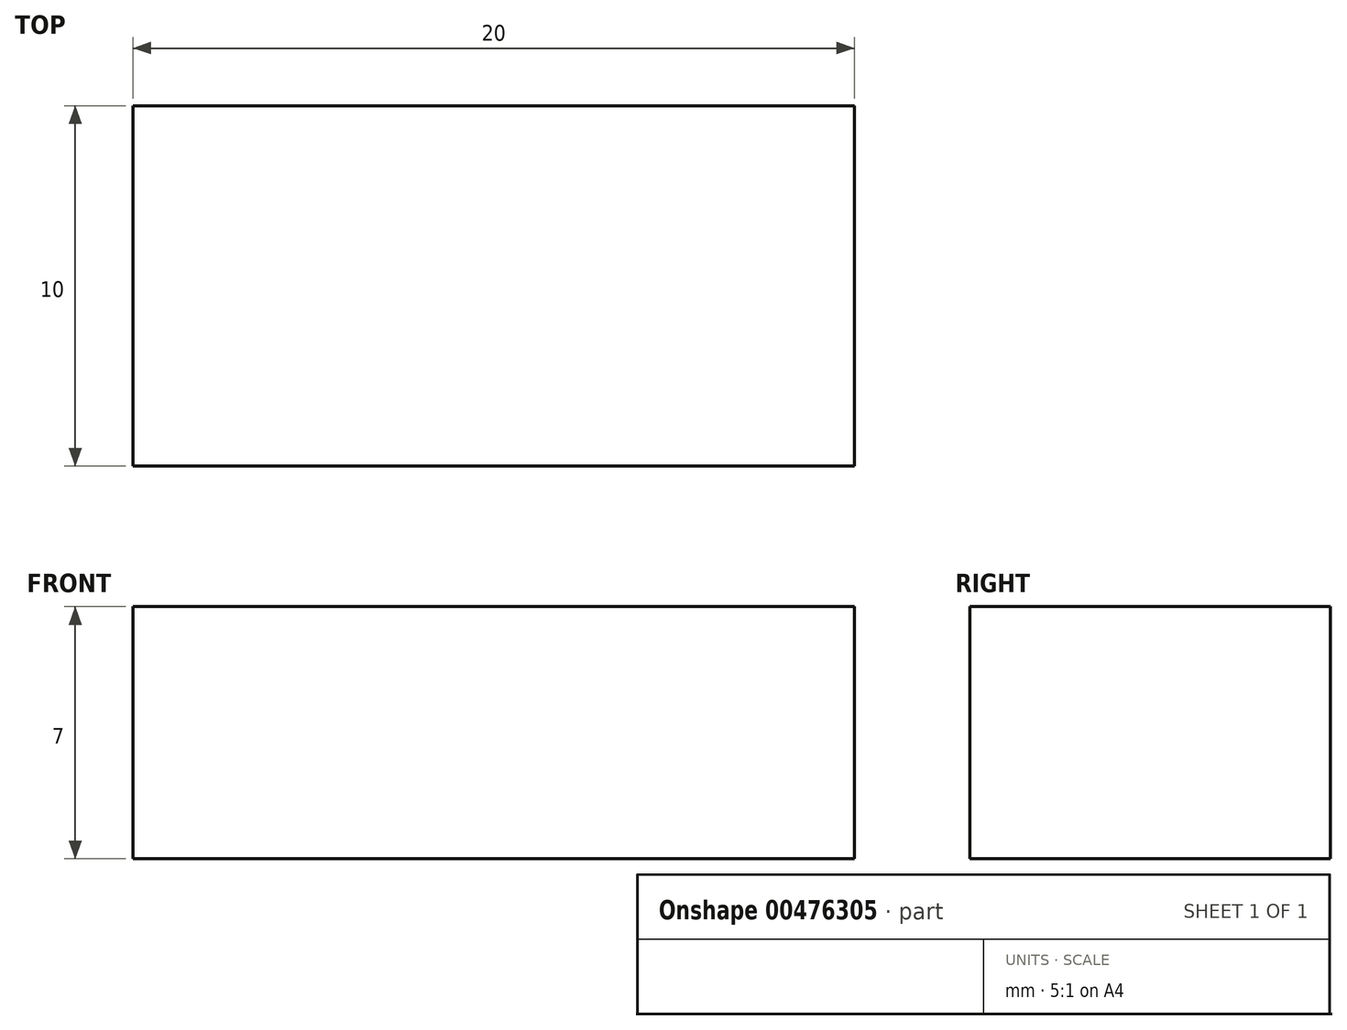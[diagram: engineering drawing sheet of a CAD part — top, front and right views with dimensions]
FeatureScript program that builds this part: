
annotation { "Feature Type Name" : "Feature", "Feature Type Description" : "" }
export const myFeature = defineFeature(function(context is Context, id is Id, definition is map)
    precondition{}
    {
        {
            var Q0;
            Q0=qCreatedBy(makeId("Top.planeOp"),FACE);
            var sketch = newSketch(context, id + "F0", { "sketchPlane" : qUnion([Q0])});
            skLineSegment(sketch, "E0.bottom", {"start": v(10, 5) * mm, "end": v(-10, 5) * mm});
            skLineSegment(sketch, "E0.top", {"start": v(10, -5) * mm, "end": v(-10, -5) * mm});
            skLineSegment(sketch, "E0.left", {"start": v(10, 5) * mm, "end": v(10, -5) * mm});
            skLineSegment(sketch, "E0.right", {"start": v(-10, 5) * mm, "end": v(-10, -5) * mm});
            skPoint(sketch, "E0.middle", {"position": v(0, 0) * mm});
            skSolve(sketch);
        }
        {
            var Q0;
            Q0=makeQuery(id+"F0.imprint","IMPRINT",FACE,{"disambiguationData":[TD([[makeQuery(id+"F0.imprint","IMPRINT",EDGE,{"derivedFrom":sQuery(id+"F0.wireOp",EDGE,"E0.bottom")}),1.0]])]});
            extrude(context, id + "F1", {"entities" : qUnion([Q0]), "depth" : 7 * mm});
        }
    });
